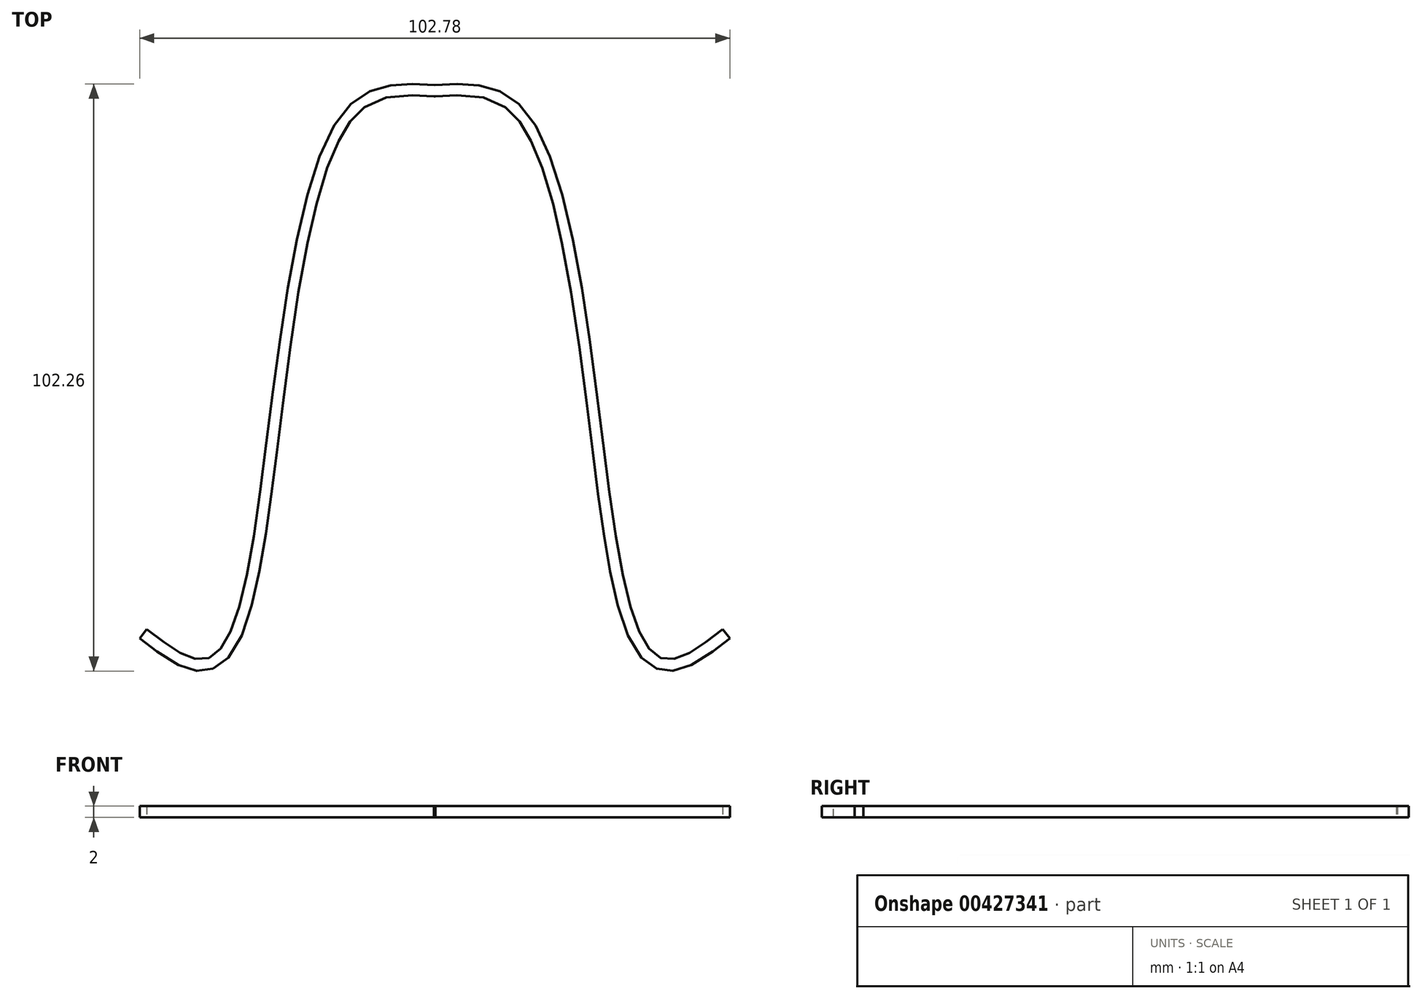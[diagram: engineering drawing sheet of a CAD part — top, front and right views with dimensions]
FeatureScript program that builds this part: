
annotation { "Feature Type Name" : "Feature", "Feature Type Description" : "" }
export const myFeature = defineFeature(function(context is Context, id is Id, definition is map)
    precondition{}
    {
        {
            var Q0;
            Q0=qCreatedBy(makeId("Top.planeOp"),FACE);
            var sketch = newSketch(context, id + "F0", { "sketchPlane" : qUnion([Q0])});
            skPoint(sketch, "E0", {"position": v(0, 100) * mm});
            skPoint(sketch, "E1", {"position": v(-40, 0) * mm});
            skFitSpline(sketch, "E2", {"points": [v(-50.15, 5.18) * mm, v(-40, 0) * mm, v(-31.67, 20.58) * mm, v(-16.27, 94.89) * mm, v(0, 100) * mm], "startDerivative": vector(68.02, -53.41) * mm, "endDerivative": vector(90.27, -5.04) * mm});
            skFitSpline(sketch, "E3.MirrorCS", {"points": [v(50.15, 5.18) * mm, v(40, 0) * mm, v(31.67, 20.58) * mm, v(16.27, 94.89) * mm, v(0, 100) * mm], "startDerivative": vector(-68.02, -53.41) * mm, "endDerivative": vector(-90.27, -5.04) * mm});
            skFitSpline(sketch, "E4.0", {"points": [v(-51.39, 3.6) * mm, v(-50.68, 3.05) * mm, v(-49.25, 1.93) * mm, v(-47.06, 0.34) * mm, v(-45.22, -0.78) * mm, v(-43.7, -1.47) * mm, v(-42.54, -1.86) * mm, v(-41.31, -2.08) * mm, v(-40.25, -2.08) * mm, v(-39.38, -1.92) * mm, v(-38.55, -1.67) * mm, v(-37.58, -1.18) * mm, v(-36.56, -0.37) * mm, v(-35.38, 0.94) * mm, v(-34.16, 2.94) * mm, v(-32.93, 5.9) * mm, v(-31.85, 9.46) * mm, v(-30.89, 13.6) * mm, v(-30, 18.3) * mm, v(-29.17, 23.57) * mm, v(-28.37, 29.3) * mm, v(-27.59, 35.4) * mm, v(-26.52, 43.88) * mm, v(-25.12, 54.84) * mm, v(-23.48, 65.55) * mm, v(-21.94, 73.5) * mm, v(-20.66, 79.06) * mm, v(-19.24, 84.07) * mm, v(-17.92, 87.69) * mm, v(-16.8, 90.18) * mm, v(-15.93, 91.84) * mm, v(-15.02, 93.26) * mm, v(-14.1, 94.42) * mm, v(-13.16, 95.38) * mm, v(-11.87, 96.4) * mm, v(-10.18, 97.3) * mm, v(-7.97, 97.91) * mm, v(-5.53, 98.17) * mm, v(-2.9, 98.16) * mm, v(-1.05, 98.06) * mm, v(-0.11, 98) * mm]});
            skFitSpline(sketch, "E5.0", {"points": [v(51.39, 3.6) * mm, v(50.68, 3.05) * mm, v(49.25, 1.93) * mm, v(47.06, 0.34) * mm, v(45.22, -0.78) * mm, v(43.7, -1.47) * mm, v(42.54, -1.86) * mm, v(41.31, -2.08) * mm, v(40.25, -2.08) * mm, v(39.38, -1.92) * mm, v(38.55, -1.67) * mm, v(37.58, -1.18) * mm, v(36.56, -0.37) * mm, v(35.38, 0.94) * mm, v(34.16, 2.94) * mm, v(32.93, 5.9) * mm, v(31.85, 9.46) * mm, v(30.89, 13.6) * mm, v(30, 18.3) * mm, v(29.17, 23.57) * mm, v(28.37, 29.3) * mm, v(27.59, 35.4) * mm, v(26.52, 43.88) * mm, v(25.12, 54.84) * mm, v(23.48, 65.55) * mm, v(21.94, 73.5) * mm, v(20.66, 79.06) * mm, v(19.24, 84.07) * mm, v(17.92, 87.69) * mm, v(16.8, 90.18) * mm, v(15.93, 91.84) * mm, v(15.02, 93.26) * mm, v(14.1, 94.42) * mm, v(13.16, 95.38) * mm, v(11.87, 96.4) * mm, v(10.18, 97.3) * mm, v(7.97, 97.91) * mm, v(5.53, 98.17) * mm, v(2.9, 98.16) * mm, v(1.05, 98.06) * mm, v(0.11, 98) * mm]});
            skLineSegment(sketch, "E6", {"start": v(-51.39, 3.6) * mm, "end": v(-50.15, 5.18) * mm});
            skLineSegment(sketch, "E7", {"start": v(50.15, 5.18) * mm, "end": v(51.39, 3.6) * mm});
            skLineSegment(sketch, "E8", {"start": v(-0.11, 98) * mm, "end": v(0.11, 98) * mm});
            skSolve(sketch);
        }
        {
            var Q0;
            Q0 = qSketchRegion(id + "F0", true);
            extrude(context, id + "F1", {"entities" : qUnion([Q0]), "depth" : 2 * mm});
        }
        {
            var Q0;
            Q0=qCreatedBy(makeId("Top.planeOp"),FACE);
            cPlane(context, id + "F2", {"entities" : qUnion([Q0]), "cplaneType" : CPlaneType.OFFSET, "offset" : 15 * mm, "width" : 150 * mm, "height" : 150 * mm});
        }
    });
